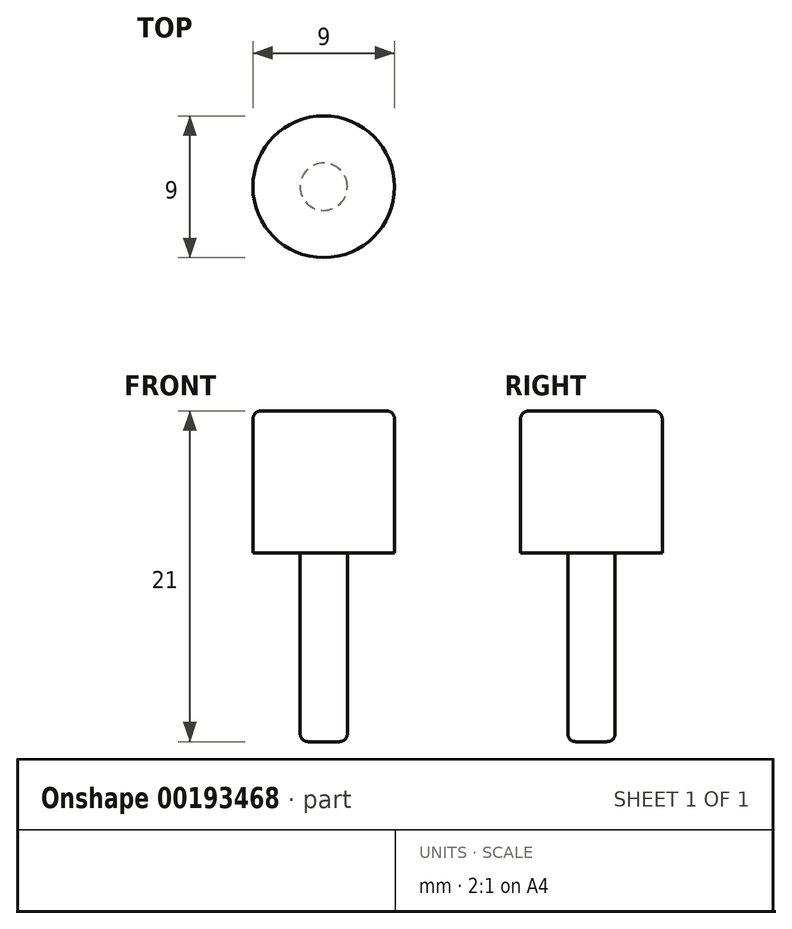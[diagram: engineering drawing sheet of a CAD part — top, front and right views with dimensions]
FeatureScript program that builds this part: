
annotation { "Feature Type Name" : "Feature", "Feature Type Description" : "" }
export const myFeature = defineFeature(function(context is Context, id is Id, definition is map)
    precondition{}
    {
        {
            var Q0;
            Q0=qCreatedBy(makeId("Top.planeOp"),FACE);
            var sketch = newSketch(context, id + "F1", { "sketchPlane" : qUnion([Q0])});
            skCircle(sketch, "E0", {"center": v(0, 0) * mm, "radius": 4.5 * mm});
            skSolve(sketch);
        }
        {
            var Q0;
            Q0 = qSketchRegion(id + "F1", true);
            extrude(context, id + "F2", {"entities" : qUnion([Q0]), "depth" : 9 * mm});
        }
        {
            var Q0;
            Q0=makeQuery(id+"F2.opExtrude","CAP_FACE",FACE,{"disambiguationData":[OSD([sQuery(id+"F1.wireOp",EDGE,"E0")])],"isStart":true});
            var sketch = newSketch(context, id + "F3", { "sketchPlane" : qUnion([Q0])});
            skCircle(sketch, "E1", {"center": v(0, 0) * mm, "radius": 1.5 * mm});
            skSolve(sketch);
        }
        {
            var Q0;
            Q0=makeQuery(id+"F3.imprint","IMPRINT",FACE,{"disambiguationData":[TD([[makeQuery(id+"F3.imprint","IMPRINT",EDGE,{"derivedFrom":sQuery(id+"F3.wireOp",EDGE,"E1")}),1.0]])]});
            var Q1;
            Q1=sQuery(id+"F3.wireOp",EDGE,"E1");
            extrude(context, id + "F4", {"entities" : qUnion([Q0]), "operationType" : NewBodyOperationType.ADD, "surfaceEntities" : qUnion([Q1]), "depth" : 12 * mm});
        }
        {
            var Q0;
            Q0=makeQuery(id+"F2.opExtrude","CAP_EDGE",EDGE,{"disambiguationData":[OSD([sQuery(id+"F1.wireOp",EDGE,"E0")])],"isStart":false});
            var Q1;
            Q1=makeQuery(id+"F4.opExtrude","CAP_EDGE",EDGE,{"disambiguationData":[OSD([sQuery(id+"F3.wireOp",EDGE,"E1")])],"isStart":false});
            fillet(context, id + "F0", {"entities" : qUnion([Q0, Q1]), "radius" : 0.5 * mm, "tangentPropagation" : true, "allowEdgeOverflow" : false});
        }
    });
